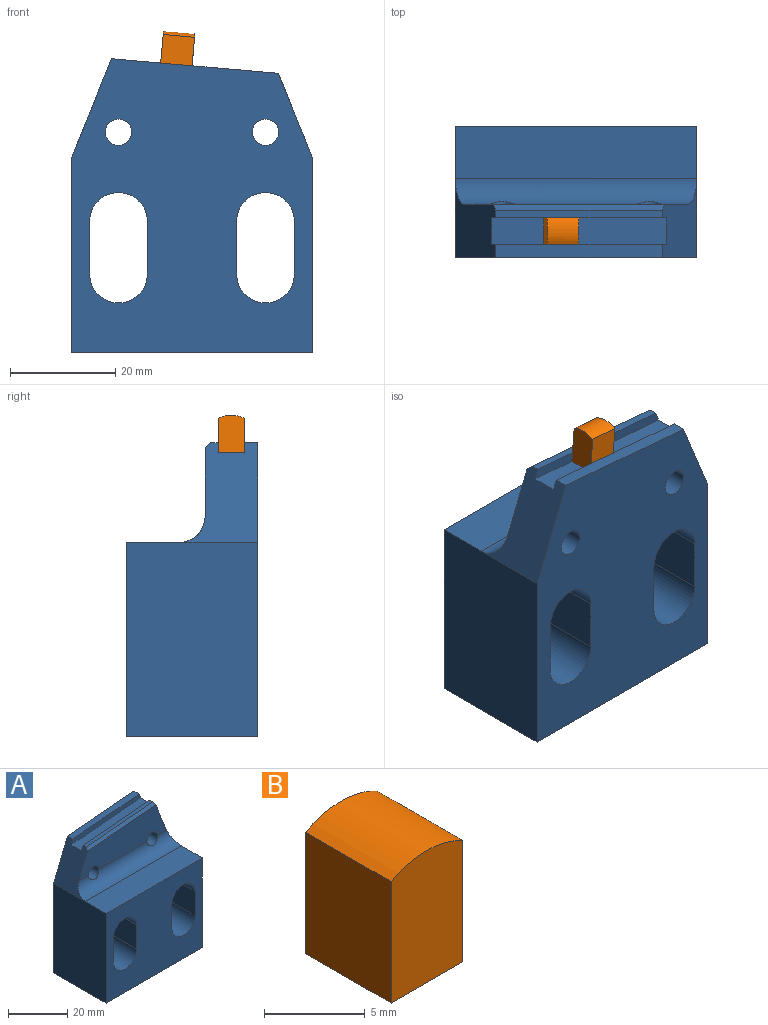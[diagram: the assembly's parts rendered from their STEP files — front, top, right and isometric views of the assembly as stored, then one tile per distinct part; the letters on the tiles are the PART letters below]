
ASSEMBLY  parts=2 mates=1
PART A: 26 faces, bbox 46x25x56 mm
  f0: plane 31.77x2.78mm, normal (-0.09,0,1), area 79.7mm2, adj f1,f10,f21,f23
  f1: plane 56x46mm, normal (0,1,0), area 1938.2mm2, adj f0,f6,f7,f8,f10,f11,f12,f13
  f2: plane 41.96x13.03mm, normal (0,-1,0), area 413.7mm2, adj f3,f10,f11,f12,f21,f25
  f3: cylinder r=5mm len=46mm, axis (-1,0,0), area 329.4mm2, adj f2,f4,f10,f11,f12,f21
  f4: plane 46x10mm, normal (0,0,1), area 460mm2, adj f3,f5,f7,f8
  f5: plane 46x37mm, normal (0,-1,0), area 1291.9mm2, adj f4,f6,f7,f8,f13,f14,f15,f16
  f6: plane 46x25mm, normal (0,0,-1), area 1150mm2, adj f1,f5,f7,f8
  f7: plane 37x25mm, normal (1,0,0), area 925mm2, adj f1,f4,f5,f6,f21
  f8: plane 37x25mm, normal (-1,0,0), area 925mm2, adj f1,f4,f5,f6,f10
  f9: plane 31.77x2.78mm, normal (-0.09,0,1), area 47.8mm2, adj f10,f21,f22,f25
  f10: plane 16.22x15mm, normal (-0.93,0,0.37), area 169.4mm2, adj f0,f1,f2,f3,f8,f9,f22,f23
  f11: cylinder r=2.5mm len=10.67mm, axis (0,1,0), area 159.7mm2, adj f1,f2,f3
  f12: cylinder r=2.5mm len=10.67mm, axis (0,1,0), area 159.7mm2, adj f1,f2,f3
  f13: plane 25x10mm, normal (1,0,0), area 250mm2, adj f1,f5,f14,f16
  f14: cylinder r=5.5mm len=25mm, axis (0,1,0), area 432mm2, adj f1,f5,f13,f15
  f15: plane 25x10mm, normal (-1,0,0), area 250mm2, adj f1,f5,f14,f16
  f16: cylinder r=5.5mm len=25mm, axis (0,1,0), area 432mm2, adj f1,f5,f13,f15
  f17: plane 25x10mm, normal (1,0,0), area 250mm2, adj f1,f5,f18,f20
  f18: cylinder r=5.5mm len=25mm, axis (0,1,0), area 432mm2, adj f1,f5,f17,f19
  f19: plane 25x10mm, normal (-1,0,0), area 250mm2, adj f1,f5,f18,f20
  f20: cylinder r=5.5mm len=25mm, axis (0,1,0), area 432mm2, adj f1,f5,f17,f19
  f21: plane 19x15mm, normal (0.93,0,0.37), area 200.2mm2, adj f0,f1,f2,f3,f7,f9,f22,f23
  f22: plane 33.32x4.77mm, normal (0,1,0), area 62.5mm2, adj f9,f10,f21,f24
  f23: plane 33.32x4.77mm, normal (0,-1,0), area 62.5mm2, adj f0,f10,f21,f24
  f24: plane 33.32x5mm, normal (-0.09,0,1), area 167.3mm2, adj f10,f21,f22,f23
  f25: plane 32.58x3.82mm, normal (-0.06,-0.71,0.7), area 45.7mm2, adj f2,f9,f10,f21
PART B: 6 faces, bbox 5x6x8 mm
  f0: cylinder r=5.2mm len=6mm, axis (0,1,0), area 31.3mm2, adj f1,f3,f4,f5
  f1: plane 7.36x6mm, normal (-1,0,0), area 44.2mm2, adj f0,f2,f4,f5
  f2: plane 6x5mm, normal (0,0,-1), area 30mm2, adj f1,f3,f4,f5
  f3: plane 7.36x6mm, normal (1,0,0), area 44.2mm2, adj f0,f2,f4,f5
  f4: plane 8x5mm, normal (0,-1,0), area 39mm2, adj f0,f1,f2,f3
  f5: plane 8x5mm, normal (0,1,0), area 39mm2, adj f0,f1,f2,f3
PLACE A rot(axis=(0,0,1),180deg) t=(-10.87,-41.21,-56.85)mm fixed
PLACE B rot(axis=(-0.04,0.04,-1),90.1deg) t=(-33.61,-44.59,-11.85)mm
MATE fastened B.f2 <-> A.f24  axis (-0.09,0,-1) through (-37.01,-18.85,-16.34)mm
